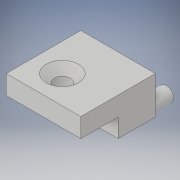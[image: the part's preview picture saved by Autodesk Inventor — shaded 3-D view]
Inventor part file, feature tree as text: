
AUTODESK INVENTOR PART (.ipt)
format: ipt  version: 2019 (Build 230136000, 136)  size: 141,312 bytes
history: native  units: mm
features: sketch x4, extrude x3, hole x1
ambient origin geometry x8: Origin, YZ Plane, XZ Plane, XY Plane, X Axis, Y Axis, Z Axis, Center Point
bodies: Solid1 (feature_tree)
feature tree (8):
  extrude  "Base"  Depth=25.4mm
  extrude  "Extrusion5"  Depth=6.35mm
  hole  "Hole3"  [1 undecoded]
  extrude  "Extrusion6"  Depth=6.35mm TaperAngle=0.0deg
  sketch  "Sketch2"  dims[d2=25.4mm d3=25.4mm]
  sketch  "Sketch10"  dims[d4=6.5mm d5=0.0mm d44=6.35mm]
  sketch  "Sketch11"  dims[d45=12.7mm d46=6.35mm]
  sketch  "Sketch12"  dims[d47=6.35mm d48=6.35mm d49=0.0mm d50=13.5mm d51=45.0deg d52=11.0mm d53=5.5mm d54=6.0mm d55=11.0mm d56=2.0mm d57=90.0deg d58=8.0mm d59=20.594885mm d60=5.0mm d61=5.0mm d62=4.85mm d63=6.25mm d64=0.0mm d32=1.0mm d33=1.0mm d34=1.0mm d35=0.15mm d36=0.25mm d37=0.375mm d38=14.3117mm d39=0.75mm d40=20.594885mm d41=0.0625mm d42=0.75mm d43=0.375mm]
note: 1 required parameter value undecoded (feature->parameter linkage not recoverable at this tier; creation-order binding heuristic only, values carry confidence <= 0.55)
